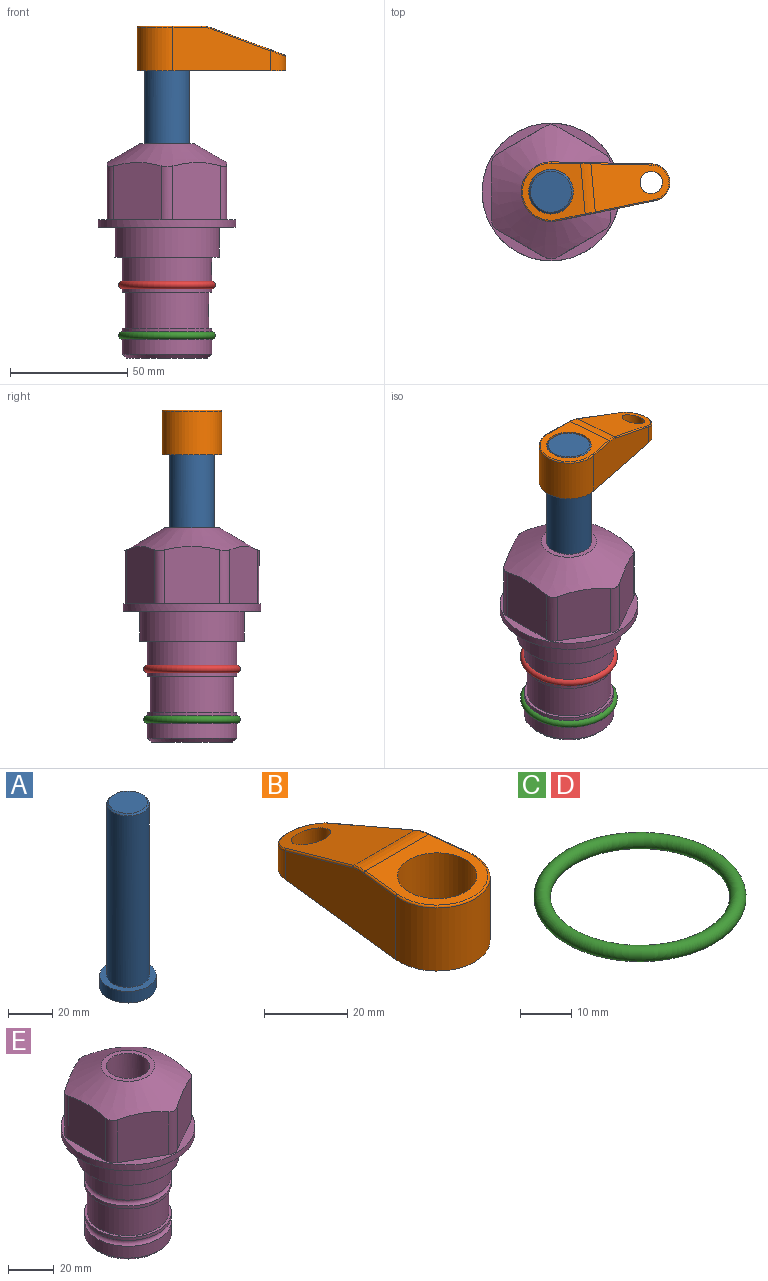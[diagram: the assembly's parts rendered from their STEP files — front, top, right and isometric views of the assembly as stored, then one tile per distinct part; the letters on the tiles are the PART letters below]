
ASSEMBLY  parts=5 mates=3
PART A: 6 faces, bbox 25.4x25.4x101.6 mm
  f0: plane 17.46x17.46mm, normal (0,0,1), area 239.5mm2, adj f5
  f1: plane 25.4x25.4mm, normal (0,0,-1), area 506.7mm2, adj f2
  f2: cylinder r=12.7mm len=25.4mm, axis (0,0,1), area 506.7mm2, adj f1,f3
  f3: plane 25.4x25.4mm, normal (0,0,1), area 221.7mm2, adj f2,f4
  f4: cylinder r=9.53mm len=94.46mm, axis (0,0,1), area 5653mm2, adj f3,f5
  f5: cone r=8.73mm half-angle=45deg, axis (0,0,-1), area 64.4mm2, adj f0,f4
PART B: 44 faces, bbox 27.5x64.5x19.1 mm
  f0: plane 2.3x0.95mm, normal (0,0,-1), area 1mm2, adj f25,f30,f34
  f1: plane 63.5x25.4mm, normal (0,0,-1), area 561.7mm2, adj f2,f3,f4,f5,f6,f7,f19,f20
  f2: cylinder r=12.7mm len=25.4mm, axis (0,0,-1), area 792.2mm2, adj f1,f3,f5,f13
  f3: plane 42.33x18.54mm, normal (0.99,0.11,0), area 647mm2, adj f1,f2,f4,f11,f12,f14
  f4: cylinder r=7.94mm len=15.78mm, axis (0,0,-1), area 158.6mm2, adj f1,f3,f5,f16
  f5: plane 42.33x18.54mm, normal (-0.99,0.11,0), area 647mm2, adj f1,f2,f4,f15,f17,f18
  f6: cylinder r=9.53mm len=19.05mm, axis (0,0,-1), area 1140.1mm2, adj f1,f8
  f7: cylinder r=4.76mm len=10.98mm, axis (0,0,-1), area 276.1mm2, adj f1,f9
  f8: plane 25.83x24.38mm, normal (0,0,1), area 262.2mm2, adj f6,f10,f11,f13,f15
  f9: plane 32.49x20.55mm, normal (0,0.34,0.94), area 489.9mm2, adj f7,f10,f14,f16,f18
  f10: cylinder r=12.7mm len=21.49mm, axis (-1,0,0), area 93.2mm2, adj f8,f9,f12,f17
  f11: cylinder r=0.51mm len=12.34mm, axis (0.11,-0.99,0), area 9.9mm2, adj f3,f8,f12,f13
  f12: bspline ~7.62x1.64mm, area 3.5mm2, adj f3,f10,f11,f14
  f13: torus R=12.19mm, axis (0,0,1), area 33.6mm2, adj f2,f8,f11,f15
  f14: cylinder r=0.51mm len=26.01mm, axis (0.1,-0.93,0.34), area 21.6mm2, adj f3,f9,f12,f16
  f15: cylinder r=0.51mm len=12.34mm, axis (0.11,0.99,0), area 9.9mm2, adj f5,f8,f13,f17
  f16: bspline ~15.78x7.05mm, area 15.7mm2, adj f4,f9,f14,f18
  f17: bspline ~7.62x1.64mm, area 3.5mm2, adj f5,f10,f15,f18
  f18: cylinder r=0.51mm len=26.01mm, axis (0.1,0.93,-0.34), area 21.6mm2, adj f5,f9,f16,f17
  f19: plane 21.6x14.29mm, normal (-0.99,-0.11,0), area 242.6mm2, adj f1,f26,f28,f34,f36,f38
  f20: plane 21.6x14.29mm, normal (0.99,-0.11,0), area 242.6mm2, adj f1,f27,f29,f37,f39,f41
  f21: cylinder r=12.7mm len=14.29mm, axis (0,0,-1), area 173.2mm2, adj f1,f26,f27,f30,f31,f33
  f22: cylinder r=7.94mm len=7.63mm, axis (0,0,-1), area 53.8mm2, adj f1,f28,f29,f42
  f23: plane 2.3x0.95mm, normal (0,0,-1), area 1mm2, adj f25,f33,f37
  f24: plane 17.94x12.32mm, normal (0,-0.34,-0.94), area 191.2mm2, adj f25,f38,f41,f42
  f25: cylinder r=9.53mm len=12.93mm, axis (-1,0,0), area 37.5mm2, adj f0,f23,f24,f31,f36,f39
  f26: cylinder r=1.59mm len=14.29mm, axis (0,0,-1), area 49mm2, adj f1,f19,f21,f32
  f27: cylinder r=1.59mm len=14.29mm, axis (0,0,-1), area 49mm2, adj f1,f20,f21,f35
  f28: cylinder r=1.59mm len=7.28mm, axis (0,0,-1), area 22.1mm2, adj f1,f19,f22,f40
  f29: cylinder r=1.59mm len=7.28mm, axis (0,0,-1), area 22.1mm2, adj f1,f20,f22,f43
  f30: torus R=14.29mm, axis (0,0,1), area 5.8mm2, adj f0,f21,f31,f32
  f31: bspline ~11.06x2.73mm, area 20.8mm2, adj f21,f25,f30,f33
  f32: sphere r=1.59mm, area 5.4mm2, adj f26,f30,f34
  f33: torus R=14.29mm, axis (0,0,1), area 5.8mm2, adj f21,f23,f31,f35
  f34: cylinder r=1.59mm len=1.68mm, axis (-0.11,0.99,0), area 2.4mm2, adj f0,f19,f32,f36
  f35: sphere r=1.59mm, area 5.4mm2, adj f27,f33,f37
  f36: bspline ~5.82x2.33mm, area 7.7mm2, adj f19,f25,f34,f38
  f37: cylinder r=1.59mm len=1.68mm, axis (0.11,0.99,0), area 2.4mm2, adj f20,f23,f35,f39
  f38: cylinder r=1.59mm len=18.33mm, axis (0.1,-0.93,0.34), area 46.7mm2, adj f19,f24,f36,f40
  f39: bspline ~5.82x2.33mm, area 7.7mm2, adj f20,f25,f37,f41
  f40: sphere r=1.59mm, area 3.6mm2, adj f28,f38,f42
  f41: cylinder r=1.59mm len=18.33mm, axis (0.1,0.93,-0.34), area 46.7mm2, adj f20,f24,f39,f43
  f42: bspline ~8.31x1.84mm, area 15.3mm2, adj f22,f24,f40,f43
  f43: sphere r=1.59mm, area 3.6mm2, adj f29,f41,f42
PART C: 1 faces, bbox 44.7x44.7x3.2 mm
  f0: torus R=19.05mm, axis (0,0,1), area 1193.9mm2
PART D: same geometry as C
PART E: 36 faces, bbox 58.7x58.7x91.2 mm
  f0: cylinder r=17.78mm len=35.56mm, axis (0,0,1), area 1670.8mm2, adj f23,f24,f31
  f1: cylinder r=19.05mm len=38.1mm, axis (0,0,1), area 1191.9mm2, adj f26,f27,f30
  f2: plane 58.66x58.66mm, normal (0,0,-1), area 1150.6mm2, adj f3,f28
  f3: cylinder r=29.33mm len=58.66mm, axis (0,0,-1), area 585.1mm2, adj f2,f4
  f4: plane 58.66x58.66mm, normal (0,0,1), area 475.9mm2, adj f3,f5,f6,f7,f8,f9,f10,f11
  f5: plane 24.5x20.32mm, normal (-0.5,0.87,0), area 562.8mm2, adj f4,f15,f16,f17
  f6: plane 24.5x20.32mm, normal (0.5,0.87,0), area 562.8mm2, adj f4,f14,f15,f17
  f7: plane 24.5x23.48mm, normal (1,0,0), area 562.8mm2, adj f4,f13,f14,f17
  f8: plane 24.5x20.32mm, normal (0.5,-0.87,0), area 562.8mm2, adj f4,f12,f13,f17
  f9: plane 24.5x20.32mm, normal (-0.5,-0.87,0), area 562.8mm2, adj f4,f11,f12,f17
  f10: plane 24.5x23.48mm, normal (-1,0,0), area 562.8mm2, adj f4,f11,f16,f17
  f11: cylinder r=5.08mm len=23.01mm, axis (0,0,-1), area 121.2mm2, adj f4,f9,f10,f17
  f12: cylinder r=5.08mm len=23.01mm, axis (0,0,-1), area 121.2mm2, adj f4,f8,f9,f17
  f13: cylinder r=5.08mm len=23.01mm, axis (0,0,-1), area 121.2mm2, adj f4,f7,f8,f17
  f14: cylinder r=5.08mm len=23.01mm, axis (0,0,-1), area 121.2mm2, adj f4,f6,f7,f17
  f15: cylinder r=5.08mm len=23.01mm, axis (0,0,-1), area 121.2mm2, adj f4,f5,f6,f17
  f16: cylinder r=5.08mm len=23.01mm, axis (0,0,-1), area 121.2mm2, adj f4,f5,f10,f17
  f17: cone r=11.73mm half-angle=60deg, axis (0,0,-1), area 2071.8mm2, adj f5,f6,f7,f8,f9,f10,f11,f12
  f18: plane 23.46x23.46mm, normal (0,0,1), area 147.4mm2, adj f17,f35
  f19: plane 34.93x34.93mm, normal (0,0,-1), area 958mm2, adj f29
  f20: cylinder r=19.05mm len=38.1mm, axis (0,0,1), area 760.1mm2, adj f21,f29
  f21: torus R=19.05mm, axis (0,0,1), area 565.3mm2, adj f20,f22
  f22: cylinder r=19.05mm len=38.1mm, axis (0,0,1), area 190mm2, adj f21,f23
  f23: plane 38.1x38.1mm, normal (0,0,1), area 146.9mm2, adj f0,f22
  f24: plane 38.1x38.1mm, normal (0,0,-1), area 146.9mm2, adj f0,f25
  f25: cylinder r=19.05mm len=38.1mm, axis (0,0,1), area 190mm2, adj f24,f26
  f26: torus R=19.05mm, axis (0,0,1), area 565.3mm2, adj f1,f25
  f27: plane 44.45x44.45mm, normal (0,0,-1), area 411.7mm2, adj f1,f28
  f28: cylinder r=22.23mm len=44.45mm, axis (0,0,1), area 1773.5mm2, adj f2,f27
  f29: cone r=19.05mm half-angle=45deg, axis (0,0,1), area 257.5mm2, adj f19,f20
  f30: cylinder r=3.17mm len=6.75mm, axis (-1,0,0), area 128mm2, adj f1,f33
  f31: cylinder r=3.17mm len=6.35mm, axis (-1,0,0), area 102.5mm2, adj f0,f33
  f32: plane 25.4x25.4mm, normal (0,0,1), area 506.7mm2, adj f33
  f33: cylinder r=12.7mm len=66.42mm, axis (0,0,-1), area 5236.2mm2, adj f30,f31,f32,f34
  f34: cone r=9.53mm half-angle=30deg, axis (0,0,-1), area 443.4mm2, adj f33,f35
  f35: cylinder r=9.53mm len=19.05mm, axis (0,0,-1), area 849mm2, adj f18,f34
PLACE A rot(axis=(0,0,1),5.2deg) t=(0,0,12.14)mm
PLACE B rot(axis=(0,0,-1),84.8deg) t=(0,0,66.75)mm
PLACE C t=(0,0,-21.59)mm
PLACE D at identity
PLACE E at identity fixed
MATE fastened C.f0 <-> E.f0  axis (0,0,1) through (0,0,-46.1)mm
MATE cylindrical A.f2 <-> E.f0  axis (0,0,1) through (0,0,37.78)mm
MATE fastened B.f2 <-> A.f2  axis (0,0,1) through (0,0,85.8)mm
